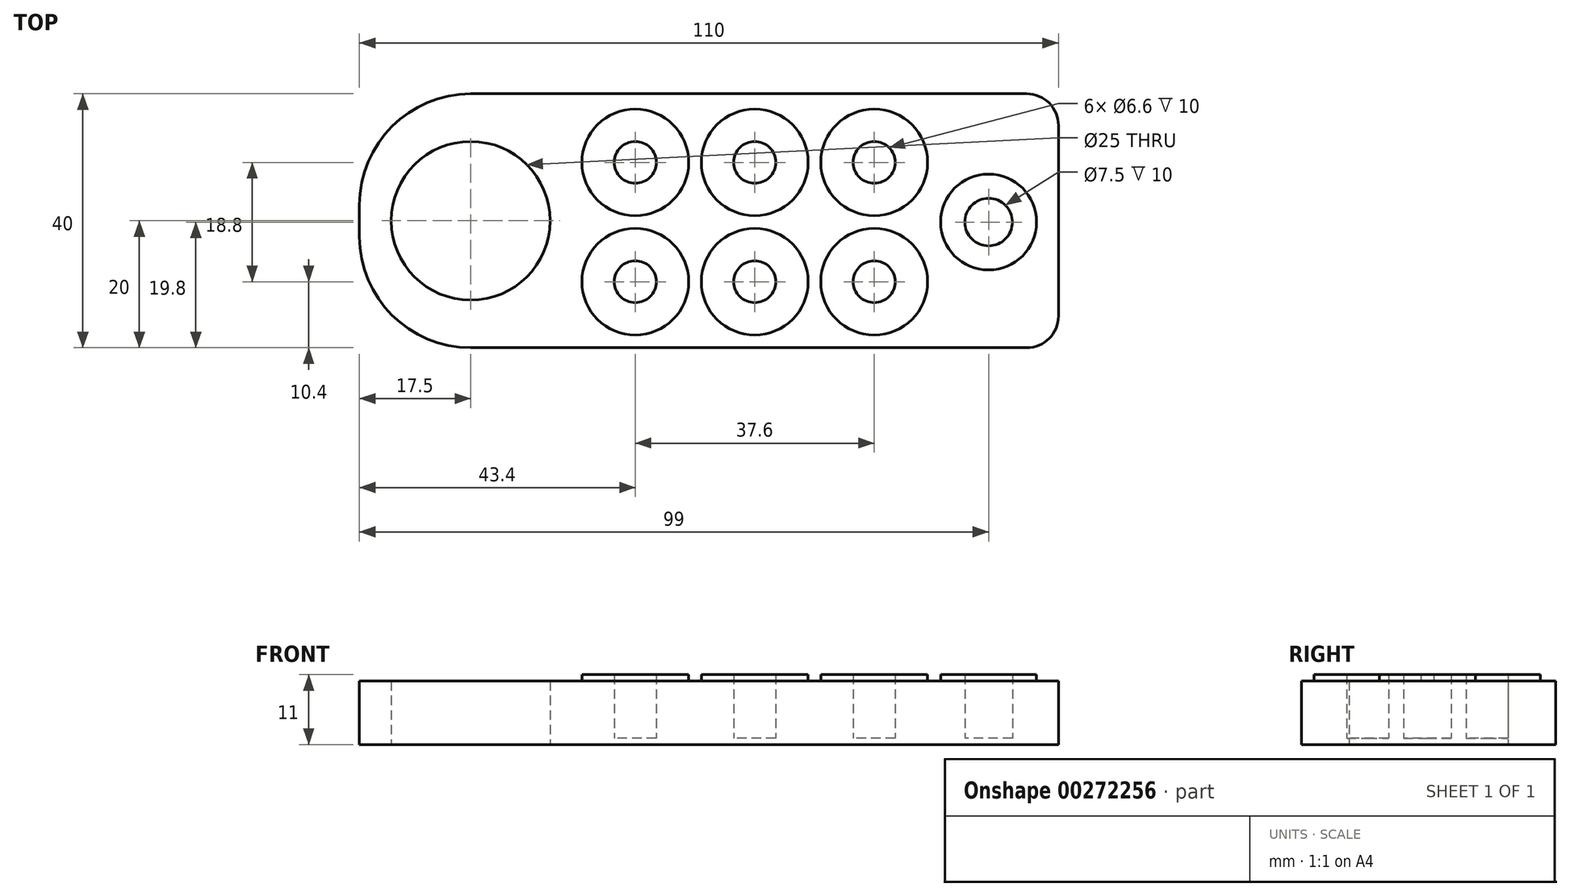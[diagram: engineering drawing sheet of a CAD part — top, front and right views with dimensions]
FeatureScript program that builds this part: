
annotation { "Feature Type Name" : "Feature", "Feature Type Description" : "" }
export const myFeature = defineFeature(function(context is Context, id is Id, definition is map)
    precondition{}
    {
        {
            var Q0;
            Q0=qCreatedBy(makeId("Top.planeOp"),FACE);
            var sketch = newSketch(context, id + "F0", { "sketchPlane" : qUnion([Q0])});
            skLineSegment(sketch, "E0.bottom", {"start": v(17.5, 0) * mm, "end": v(105, 0) * mm});
            skLineSegment(sketch, "E0.top", {"start": v(17.5, 40) * mm, "end": v(105, 40) * mm});
            skLineSegment(sketch, "E0.left", {"start": v(0, 17.5) * mm, "end": v(0, 22.5) * mm});
            skLineSegment(sketch, "E0.right", {"start": v(110, 5) * mm, "end": v(110, 35) * mm});
            skLineSegment(sketch, "E1.bottom", {"start": v(0, 0) * mm, "end": v(17.5, 0) * mm, "construction": true});
            skLineSegment(sketch, "E1.top", {"start": v(0, 20) * mm, "end": v(17.5, 20) * mm, "construction": true});
            skLineSegment(sketch, "E1.left", {"start": v(0, 0) * mm, "end": v(0, 20) * mm, "construction": true});
            skLineSegment(sketch, "E1.right", {"start": v(17.5, 0) * mm, "end": v(17.5, 20) * mm, "construction": true});
            skCircle(sketch, "E2", {"center": v(17.5, 20) * mm, "radius": 12.5 * mm});
            skPoint(sketch, "E3.visualSharp", {"position": v(0, 0) * mm});
            skArc(sketch, "E3.filletArc", {"start": v(0, 17.5) * mm, "mid": v(5.13, 5.13) * mm, "end": v(17.5, 0) * mm});
            skPoint(sketch, "E4.visualSharp", {"position": v(0, 40) * mm});
            skArc(sketch, "E4.filletArc", {"start": v(17.5, 40) * mm, "mid": v(5.13, 34.87) * mm, "end": v(0, 22.5) * mm});
            skPoint(sketch, "E5.visualSharp", {"position": v(110, 40) * mm});
            skArc(sketch, "E5.filletArc", {"start": v(110, 35) * mm, "mid": v(108.54, 38.54) * mm, "end": v(105, 40) * mm});
            skPoint(sketch, "E6.visualSharp", {"position": v(110, 0) * mm});
            skArc(sketch, "E6.filletArc", {"start": v(105, 0) * mm, "mid": v(108.54, 1.46) * mm, "end": v(110, 5) * mm});
            skSolve(sketch);
        }
        {
            var Q0;
            Q0=makeQuery(id+"F0.imprint","IMPRINT",FACE,{"disambiguationData":[TD([[makeQuery(id+"F0.imprint","IMPRINT",EDGE,{"derivedFrom":sQuery(id+"F0.wireOp",EDGE,"E0.bottom")}),1.0]])]});
            extrude(context, id + "F1", {"entities" : qUnion([Q0]), "depth" : 10 * mm});
        }
        {
            var Q0;
            Q0=makeQuery(id+"F1.opExtrude","CAP_FACE",FACE,{"disambiguationData":[OSD([sQuery(id+"F0.wireOp",EDGE,"E0.bottom"),sQuery(id+"F0.wireOp",EDGE,"E0.top"),sQuery(id+"F0.wireOp",EDGE,"E0.left"),sQuery(id+"F0.wireOp",EDGE,"E0.right"),sQuery(id+"F0.wireOp",EDGE,"E2"),sQuery(id+"F0.wireOp",EDGE,"E3.filletArc"),sQuery(id+"F0.wireOp",EDGE,"E4.filletArc"),sQuery(id+"F0.wireOp",EDGE,"E5.filletArc"),sQuery(id+"F0.wireOp",EDGE,"E6.filletArc")])],"isStart":false});
            var sketch = newSketch(context, id + "F2", { "sketchPlane" : qUnion([Q0])});
            skLineSegment(sketch, "E7.bottom", {"start": v(0, 0) * mm, "end": v(43.4, 0) * mm, "construction": true});
            skLineSegment(sketch, "E7.top", {"start": v(0, 10.4) * mm, "end": v(43.4, 10.4) * mm, "construction": true});
            skLineSegment(sketch, "E7.left", {"start": v(0, 0) * mm, "end": v(0, 10.4) * mm, "construction": true});
            skLineSegment(sketch, "E7.right", {"start": v(43.4, 0) * mm, "end": v(43.4, 10.4) * mm, "construction": true});
            skLineSegment(sketch, "E8.bottom", {"start": v(43.4, 10.4) * mm, "end": v(62.2, 10.4) * mm, "construction": true});
            skLineSegment(sketch, "E8.top", {"start": v(43.4, 29.2) * mm, "end": v(62.2, 29.2) * mm, "construction": true});
            skLineSegment(sketch, "E8.left", {"start": v(43.4, 10.4) * mm, "end": v(43.4, 29.2) * mm, "construction": true});
            skLineSegment(sketch, "E8.right", {"start": v(62.2, 10.4) * mm, "end": v(62.2, 29.2) * mm, "construction": true});
            skLineSegment(sketch, "E9.bottom", {"start": v(62.2, 29.2) * mm, "end": v(81, 29.2) * mm, "construction": true});
            skLineSegment(sketch, "E9.top", {"start": v(62.2, 10.4) * mm, "end": v(81, 10.4) * mm, "construction": true});
            skLineSegment(sketch, "E9.left", {"start": v(62.2, 29.2) * mm, "end": v(62.2, 10.4) * mm, "construction": true});
            skLineSegment(sketch, "E9.right", {"start": v(81, 29.2) * mm, "end": v(81, 10.4) * mm, "construction": true});
            skPoint(sketch, "E10.oppositeSnap0", {"position": v(81, 19.8) * mm});
            skLineSegment(sketch, "E10.bottom", {"start": v(81, 29.2) * mm, "end": v(99, 29.2) * mm, "construction": true});
            skLineSegment(sketch, "E10.top", {"start": v(81, 19.8) * mm, "end": v(99, 19.8) * mm, "construction": true});
            skLineSegment(sketch, "E10.left", {"start": v(81, 29.2) * mm, "end": v(81, 19.8) * mm, "construction": true});
            skLineSegment(sketch, "E10.right", {"start": v(99, 29.2) * mm, "end": v(99, 19.8) * mm, "construction": true});
            skCircle(sketch, "E11", {"center": v(43.4, 29.2) * mm, "radius": 8.4 * mm});
            skCircle(sketch, "E12", {"center": v(43.4, 10.4) * mm, "radius": 8.4 * mm});
            skCircle(sketch, "E13", {"center": v(62.2, 10.4) * mm, "radius": 8.4 * mm});
            skCircle(sketch, "E14", {"center": v(81, 10.4) * mm, "radius": 8.4 * mm});
            skCircle(sketch, "E15", {"center": v(81, 29.2) * mm, "radius": 8.4 * mm});
            skCircle(sketch, "E16", {"center": v(62.2, 29.2) * mm, "radius": 8.4 * mm});
            skCircle(sketch, "E17", {"center": v(62.2, 29.2) * mm, "radius": 3.3 * mm});
            skCircle(sketch, "E18", {"center": v(81, 29.2) * mm, "radius": 3.3 * mm});
            skCircle(sketch, "E19", {"center": v(81, 10.4) * mm, "radius": 3.3 * mm});
            skCircle(sketch, "E20", {"center": v(62.2, 10.4) * mm, "radius": 3.3 * mm});
            skCircle(sketch, "E21", {"center": v(43.4, 10.4) * mm, "radius": 3.3 * mm});
            skCircle(sketch, "E22", {"center": v(43.4, 29.2) * mm, "radius": 3.3 * mm});
            skCircle(sketch, "E23", {"center": v(99, 19.8) * mm, "radius": 7.55 * mm});
            skCircle(sketch, "E24", {"center": v(99, 19.8) * mm, "radius": 3.75 * mm});
            skSolve(sketch);
        }
        {
            var Q0;
            Q0=makeQuery(id+"F2.imprint","IMPRINT",FACE,{"disambiguationData":[TD([[makeQuery(id+"F2.imprint","IMPRINT",EDGE,{"derivedFrom":sQuery(id+"F2.wireOp",EDGE,"E11")}),1.0]])]});
            var Q1;
            Q1=makeQuery(id+"F2.imprint","IMPRINT",FACE,{"disambiguationData":[TD([[makeQuery(id+"F2.imprint","IMPRINT",EDGE,{"derivedFrom":sQuery(id+"F2.wireOp",EDGE,"E16")}),1.0]])]});
            var Q2;
            Q2=makeQuery(id+"F2.imprint","IMPRINT",FACE,{"disambiguationData":[TD([[makeQuery(id+"F2.imprint","IMPRINT",EDGE,{"derivedFrom":sQuery(id+"F2.wireOp",EDGE,"E13")}),1.0]])]});
            var Q3;
            Q3=makeQuery(id+"F2.imprint","IMPRINT",FACE,{"disambiguationData":[TD([[makeQuery(id+"F2.imprint","IMPRINT",EDGE,{"derivedFrom":sQuery(id+"F2.wireOp",EDGE,"E12")}),1.0]])]});
            var Q4;
            Q4=makeQuery(id+"F2.imprint","IMPRINT",FACE,{"disambiguationData":[TD([[makeQuery(id+"F2.imprint","IMPRINT",EDGE,{"derivedFrom":sQuery(id+"F2.wireOp",EDGE,"E14")}),1.0]])]});
            var Q5;
            Q5=makeQuery(id+"F2.imprint","IMPRINT",FACE,{"disambiguationData":[TD([[makeQuery(id+"F2.imprint","IMPRINT",EDGE,{"derivedFrom":sQuery(id+"F2.wireOp",EDGE,"E15")}),1.0]])]});
            var Q6;
            Q6=makeQuery(id+"F2.imprint","IMPRINT",FACE,{"disambiguationData":[TD([[makeQuery(id+"F2.imprint","IMPRINT",EDGE,{"derivedFrom":sQuery(id+"F2.wireOp",EDGE,"E23")}),1.0]])]});
            extrude(context, id + "F3", {"entities" : qUnion([Q0, Q1, Q2, Q3, Q4, Q5, Q6]), "operationType" : NewBodyOperationType.ADD, "depth" : 1 * mm});
        }
        {
            var Q0;
            Q0=makeQuery(id+"F2.imprint","IMPRINT",FACE,{"disambiguationData":[TD([[makeQuery(id+"F2.imprint","IMPRINT",EDGE,{"derivedFrom":sQuery(id+"F2.wireOp",EDGE,"E24")}),1.0]])]});
            var Q1;
            Q1=makeQuery(id+"F2.imprint","IMPRINT",FACE,{"disambiguationData":[TD([[makeQuery(id+"F2.imprint","IMPRINT",EDGE,{"derivedFrom":sQuery(id+"F2.wireOp",EDGE,"E18")}),1.0]])]});
            var Q2;
            Q2=makeQuery(id+"F2.imprint","IMPRINT",FACE,{"disambiguationData":[TD([[makeQuery(id+"F2.imprint","IMPRINT",EDGE,{"derivedFrom":sQuery(id+"F2.wireOp",EDGE,"E19")}),1.0]])]});
            var Q3;
            Q3=makeQuery(id+"F2.imprint","IMPRINT",FACE,{"disambiguationData":[TD([[makeQuery(id+"F2.imprint","IMPRINT",EDGE,{"derivedFrom":sQuery(id+"F2.wireOp",EDGE,"E20")}),1.0]])]});
            var Q4;
            Q4=makeQuery(id+"F2.imprint","IMPRINT",FACE,{"disambiguationData":[TD([[makeQuery(id+"F2.imprint","IMPRINT",EDGE,{"derivedFrom":sQuery(id+"F2.wireOp",EDGE,"E17")}),1.0]])]});
            var Q5;
            Q5=makeQuery(id+"F2.imprint","IMPRINT",FACE,{"disambiguationData":[TD([[makeQuery(id+"F2.imprint","IMPRINT",EDGE,{"derivedFrom":sQuery(id+"F2.wireOp",EDGE,"E22")}),1.0]])]});
            var Q6;
            Q6=makeQuery(id+"F2.imprint","IMPRINT",FACE,{"disambiguationData":[TD([[makeQuery(id+"F2.imprint","IMPRINT",EDGE,{"derivedFrom":sQuery(id+"F2.wireOp",EDGE,"E21")}),1.0]])]});
            extrude(context, id + "F4", {"entities" : qUnion([Q0, Q1, Q2, Q3, Q4, Q5, Q6]), "operationType" : NewBodyOperationType.REMOVE, "oppositeDirection" : true, "depth" : 9 * mm});
        }
    });
